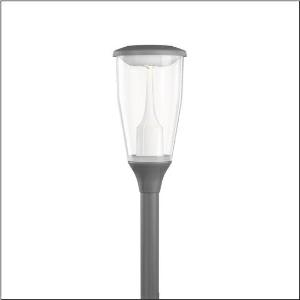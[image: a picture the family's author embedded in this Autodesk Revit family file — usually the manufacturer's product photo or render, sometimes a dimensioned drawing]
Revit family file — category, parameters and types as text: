
# Revit family: dl_11_iq___p1_0a_5xa5565nf14h000022_7674
name_source: partatom
category: Lighting Fixtures
units: mm (PartAtom-declared; Revit-internal decimal feet)

## family parameters
Cut with Voids When Loaded = No
Host = Face
Light Source = No
Part Type = Normal
Room Calculation Point = No
Round Connector Dimension = Use Diameter
Shared = No

## types (1)
- --- (1 x LED, 1530 lm, 11.8 W, 2700K)
    Apparent Load = 12 VA
    CIE Flux Codes = 34 63 91 95 100
    Color Rendering = 70
    Color Temperature = 2700K
    Default Elevation = 1800 mm
    Description = DL 11 iQ, mast luminaire, Module 540 iQ-SR, primary light control with 3 zone facetted reflector, of plastic, silver coated, highly specular, structured, primary optical cover: cover, of PMMA, transparent, light distribution: P1.0a, light emission: direct distribution, primary light characteristic: asymmetric, installation type: post-top, LED, High Power LED, rated luminous flux: 1.560lm, luminous efficacy: 149lm/W, light colour: 727, colour temperature: 2700K, control: Street-Remote, Auto-Match, Temp-Guard, Lumen-Switch, Night-Set, Smart-Wire, Light-Fading, Desk-Remote (wireless, voltage-free reading and setting of iQ features in the workshop via application-optimized NFC function/RFID function), optimised constant luminous flux control (CLO 2.0), mains connection: 220..240V, AC, 50/60Hz, connection cable pre-assembled, cable length: 5,5m, start of lifetime: 12W, end of service life: 12W, reduction: 5W, luminaire housing, upper part, of diecast aluminium, coated, Siteco® metallic grey (DB 702S), spigot size: 60mm (post-top), post-top mast mounting element, of diecast aluminium, coated, Siteco® metallic grey (DB 702S), Module 540 iQ-SR, traffic white (RAL 9016), equipment: standard, protection rating (complete): IP66, insulation class (complete): insulation class II (safety insulation), certification: CE, ENEC, ENEC+, VDE, packaging unit: 1 piece

Light Distribution: P1.0a
    Height = 665 mm
    Lamp = 1 x LED
    Lamp Light Flux = 1530 lm
    Lamp Power = 11.8 W
    Lamp count = 1
    Length = 334 mm
    Luminous efficacy = 130 lm/W
    Manufacturer = Siteco
    ModVariant = No
    Model = 5XA5565NF14H000022
    Number of Poles = 1
    OnlyDefault = Yes
    Power Factor = 1
    Product Name = DL 11 iQ | P1.0a
    Product group = mast luminaire | pylon top
    ProductGroupID = 6100
    Protection Class = Protection class II
    Protection Degree = IP 66
    RLX_Detail_Level = 1
    RLX_Emergency_Light_Flux = 0 lm
    RLX_Emergency_Type = 0
    RLX_Emergency_Type_DB = No
    RlxData = <blob elided: 103193 chars, md5=acee3266>
    Socket = socket
    Standby Power = 0 W
    System Light Flux = 1530 lm
    System Power = 12 W
    Type Comments = factory setting: luminous flux: 100 % | dim-lin: 254 | 472 mA
    Type Image = l_1258354.jpg
    URL = http://relux.com
    VarID = @adj_060601
    Voltage = 0 V
    Weight = 0.00 kg
    Width = 0 mm  [stored 0 ft]

note: [stored X ft] marks values corroborated as IEEE doubles in the binary element streams (Revit-internal decimal feet)

## geometry (parser evidence)
native form markers: Blend x4, Sweep x13
no freeform markers — native parametric forms only
